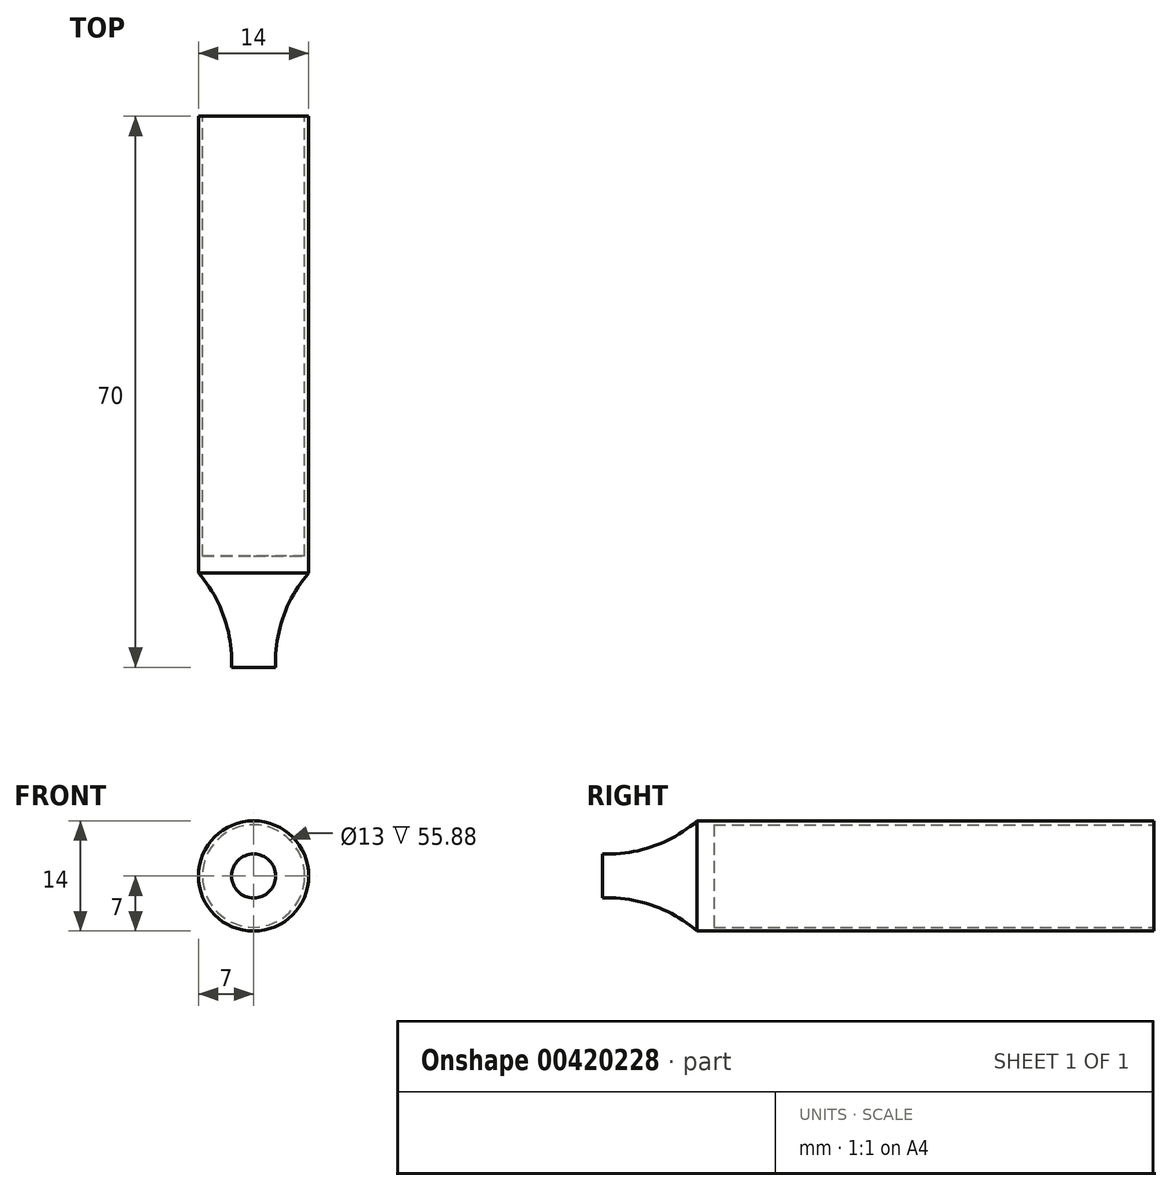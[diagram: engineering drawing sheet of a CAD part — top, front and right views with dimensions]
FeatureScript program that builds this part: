
annotation { "Feature Type Name" : "Feature", "Feature Type Description" : "" }
export const myFeature = defineFeature(function(context is Context, id is Id, definition is map)
    precondition{}
    {
        {
            var Q0;
            Q0=qCreatedBy(makeId("Top.planeOp"),FACE);
            var sketch = newSketch(context, id + "F0", { "sketchPlane" : qUnion([Q0])});
            skLineSegment(sketch, "E0", {"start": v(0, -10) * mm, "end": v(0, -34) * mm});
            skLineSegment(sketch, "E1", {"start": v(7, -10) * mm, "end": v(7, -34) * mm});
            skLineSegment(sketch, "E2", {"start": v(0, -34) * mm, "end": v(7, -34) * mm});
            skPoint(sketch, "E3.orphan", {"position": v(0, -68) * mm});
            skLineSegment(sketch, "E4.MirrorCS", {"start": v(0, -68) * mm, "end": v(0, -34) * mm});
            skArc(sketch, "E5.MirrorCS", {"start": v(0, -68) * mm, "mid": v(3.24, -73.6) * mm, "end": v(4.2, -80) * mm});
            skLineSegment(sketch, "E6.MirrorCS", {"start": v(7, -80) * mm, "end": v(4.2, -80) * mm});
            skLineSegment(sketch, "E7.MirrorCS", {"start": v(7, -80) * mm, "end": v(7, -34) * mm});
            skLineSegment(sketch, "E8", {"start": v(0, -10) * mm, "end": v(7, -10) * mm});
            skPoint(sketch, "E9.start.orphan", {"position": v(0, 0) * mm});
            skPoint(sketch, "E10.end.orphan", {"position": v(4.2, 12) * mm});
            skPoint(sketch, "E10.start.orphan", {"position": v(7, 12) * mm});
            skSolve(sketch);
        }
        {
            var Q0;
            Q0=makeQuery(id+"F0.imprint","IMPRINT",FACE,{"disambiguationData":[TD([[makeQuery(id+"F0.imprint","IMPRINT",EDGE,{"derivedFrom":sQuery(id+"F0.wireOp",EDGE,"E0")}),1.0]])]});
            var Q1;
            Q1=makeQuery(id+"F0.imprint","IMPRINT",FACE,{"disambiguationData":[TD([[makeQuery(id+"F0.imprint","IMPRINT",EDGE,{"derivedFrom":sQuery(id+"F0.wireOp",EDGE,"E2")}),-1.0]])]});
            var Q2;
            Q2=sQuery(id+"F0.wireOp",EDGE,"E1");
            revolve(context, id + "F1", {"entities" : qUnion([Q0, Q1]), "axis" : qUnion([Q2]), "revolveType" : RevolveType.FULL});
        }
        {
            var Q0;
            Q0=makeQuery(id+"F1.opRevolve","SWEPT_FACE",FACE,{"disambiguationData":[OSD([sQuery(id+"F0.wireOp",EDGE,"E8")])]});
            var sketch = newSketch(context, id + "F2", { "sketchPlane" : qUnion([Q0])});
            skCircle(sketch, "E11", {"center": v(-7, 0) * mm, "radius": 6.5 * mm});
            skSolve(sketch);
        }
        {
            var Q0;
            Q0=makeQuery(id+"F2.imprint","IMPRINT",FACE,{"disambiguationData":[TD([[makeQuery(id+"F2.imprint","IMPRINT",EDGE,{"derivedFrom":sQuery(id+"F2.wireOp",EDGE,"E11")}),1.0]])]});
            extrude(context, id + "F3", {"entities" : qUnion([Q0]), "operationType" : NewBodyOperationType.REMOVE, "oppositeDirection" : true, "depth" : 55.88 * mm, "offsetDistance" : 25.4 * mm});
        }
    });
